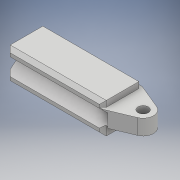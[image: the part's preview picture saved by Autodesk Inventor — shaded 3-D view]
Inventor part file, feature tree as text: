
AUTODESK INVENTOR PART (.ipt)
format: ipt  version: 2018 (Build 220112000, 112)  size: 434,176 bytes
history: native  units: mm
features: sketch x10, extrude x6, sweep x2, chamfer x2, other x1, projected_geometry x1
ambient origin geometry x8: Origin, YZ Plane, XZ Plane, XY Plane, X Axis, Y Axis, Z Axis, Center Point
bodies: Body1 (feature_tree)
feature tree (22):
  other  "ソリッド1"
  extrude  "押し出し1"  Depth=11.5mm
  extrude  "押し出し3"  Depth=9.0mm
  extrude  "押し出し4"  Depth=28.0mm TaperAngle=0.0deg
  sweep  "スイープ2"
  sweep  "スイープ3"
  extrude  "押し出し5"  Depth=2.75mm TaperAngle=0.0deg
  extrude  "押し出し6"  Depth=5.0mm
  chamfer  "面取り1"  Distance=3.0mm
  chamfer  "面取り2"  Distance=29.0mm
  extrude  "押し出し8"  Depth=1.2mm
  sketch  "スケッチ1"
  sketch  "スケッチ3"
  sketch  "スケッチ4"
  sketch  "スケッチ8"
  sketch  "スケッチ9"
  sketch  "スケッチ10"
  projected_geometry  "投影ループ1"
  sketch  "スケッチ11"
  sketch  "スケッチ12"
  sketch  "スケッチ13"
  sketch  "スケッチ15"
